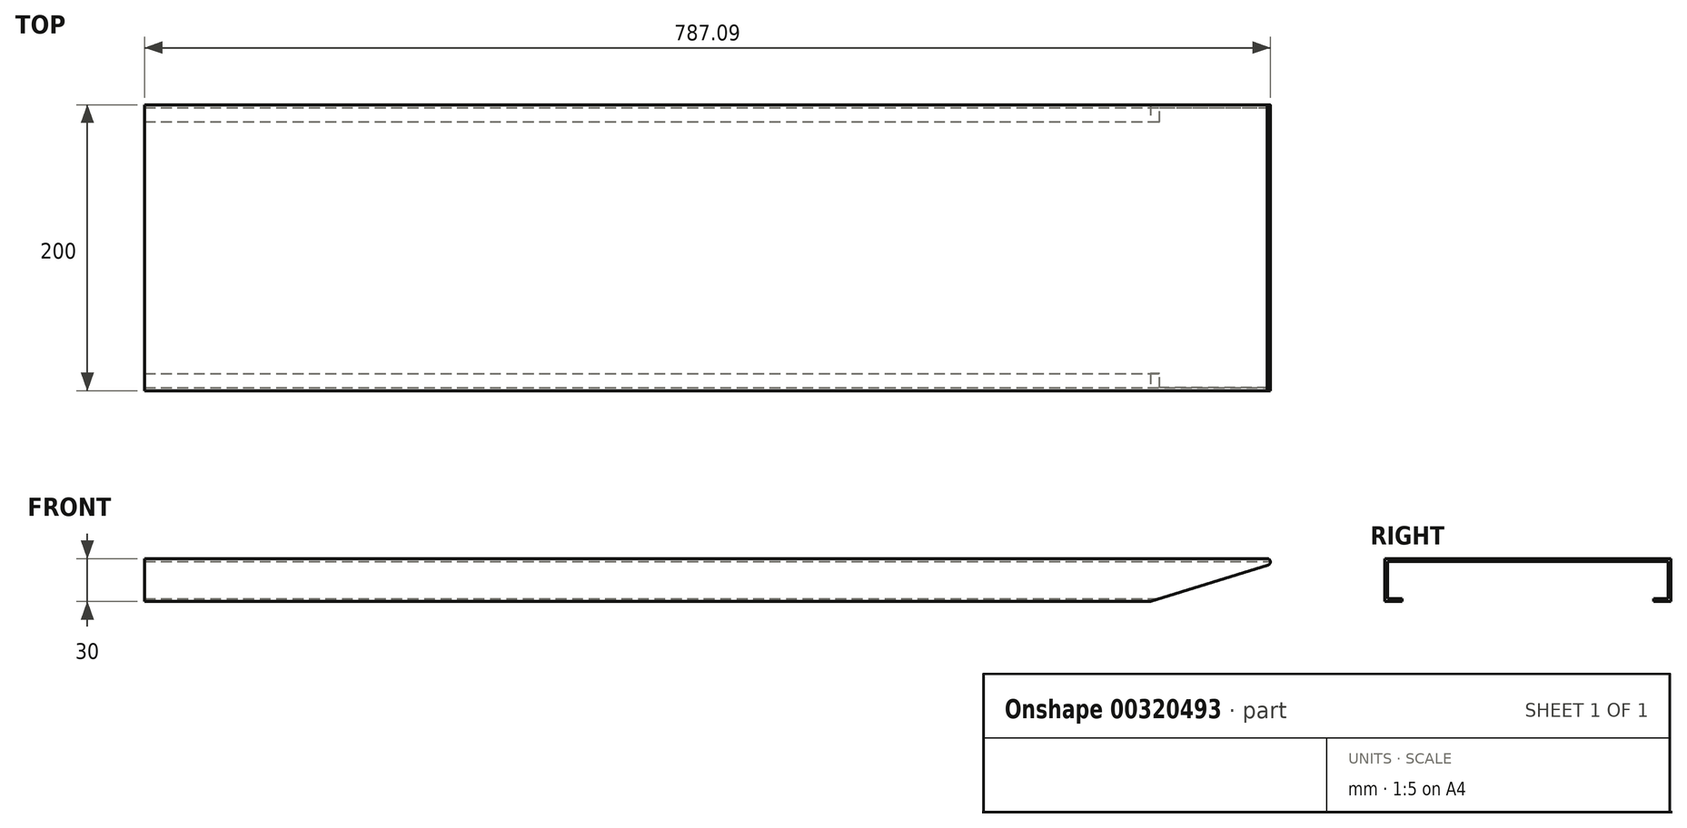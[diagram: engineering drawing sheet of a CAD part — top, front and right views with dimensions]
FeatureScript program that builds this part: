
annotation { "Feature Type Name" : "Feature", "Feature Type Description" : "" }
export const myFeature = defineFeature(function(context is Context, id is Id, definition is map)
    precondition{}
    {
        {
            var Q0;
            Q0=qCreatedBy(makeId("Right.planeOp"),FACE);
            var sketch = newSketch(context, id + "F0", { "sketchPlane" : qUnion([Q0])});
            skLineSegment(sketch, "E0", {"start": v(-91.3, -39.22) * mm, "end": v(-103.3, -39.22) * mm});
            skLineSegment(sketch, "E1", {"start": v(-103.3, -39.22) * mm, "end": v(-103.3, -9.22) * mm});
            skLineSegment(sketch, "E2", {"start": v(-103.3, -9.22) * mm, "end": v(96.7, -9.22) * mm});
            skLineSegment(sketch, "E3", {"start": v(96.7, -9.22) * mm, "end": v(96.7, -39.22) * mm});
            skLineSegment(sketch, "E4", {"start": v(96.7, -39.22) * mm, "end": v(84.7, -39.22) * mm});
            skLineSegment(sketch, "E5", {"start": v(84.7, -39.22) * mm, "end": v(84.7, -37.22) * mm});
            skLineSegment(sketch, "E6", {"start": v(84.7, -37.22) * mm, "end": v(94.7, -37.22) * mm});
            skLineSegment(sketch, "E7", {"start": v(94.7, -37.22) * mm, "end": v(94.7, -11.22) * mm});
            skLineSegment(sketch, "E8", {"start": v(94.7, -11.22) * mm, "end": v(-101.3, -11.22) * mm});
            skLineSegment(sketch, "E9", {"start": v(-101.3, -11.22) * mm, "end": v(-101.3, -37.22) * mm});
            skLineSegment(sketch, "E10", {"start": v(-101.3, -37.22) * mm, "end": v(-91.3, -37.22) * mm});
            skLineSegment(sketch, "E11", {"start": v(-91.3, -37.22) * mm, "end": v(-91.3, -39.22) * mm});
            skSolve(sketch);
        }
        {
            var Q0;
            Q0=makeQuery(id+"F0.imprint","IMPRINT",FACE,{"disambiguationData":[TD([[makeQuery(id+"F0.imprint","IMPRINT",EDGE,{"derivedFrom":sQuery(id+"F0.wireOp",EDGE,"E0")}),-1.0]])]});
            extrude(context, id + "F1", {"entities" : qUnion([Q0]), "oppositeDirection" : true, "depth" : 800 * mm});
        }
        {
            var Q0;
            Q0=makeQuery(id+"F1.opExtrude","SWEPT_FACE",FACE,{"disambiguationData":[OSD([sQuery(id+"F0.wireOp",EDGE,"E1")])]});
            var sketch = newSketch(context, id + "F2", { "sketchPlane" : qUnion([Q0])});
            skLineSegment(sketch, "E12", {"start": v(-14.53, -13.73) * mm, "end": v(-96.67, -39.22) * mm});
            skLineSegment(sketch, "E13", {"start": v(-96.67, -39.22) * mm, "end": v(0, -39.22) * mm});
            skLineSegment(sketch, "E14", {"start": v(0, -9.22) * mm, "end": v(0, -39.22) * mm});
            skArc(sketch, "E15", {"start": v(-14.53, -13.73) * mm, "mid": v(-12.92, -11.29) * mm, "end": v(-15, -9.22) * mm});
            skLineSegment(sketch, "E16", {"start": v(-15, -9.22) * mm, "end": v(0, -9.22) * mm});
            skSolve(sketch);
        }
        {
            var Q0;
            Q0=makeQuery(id+"F2.imprint","IMPRINT",FACE,{"disambiguationData":[TD([[makeQuery(id+"F2.imprint","IMPRINT",EDGE,{"derivedFrom":sQuery(id+"F2.wireOp",EDGE,"E12")}),1.0]])]});
            extrude(context, id + "F3", {"entities" : qUnion([Q0]), "operationType" : NewBodyOperationType.REMOVE, "oppositeDirection" : true, "depth" : 250 * mm});
        }
    });
